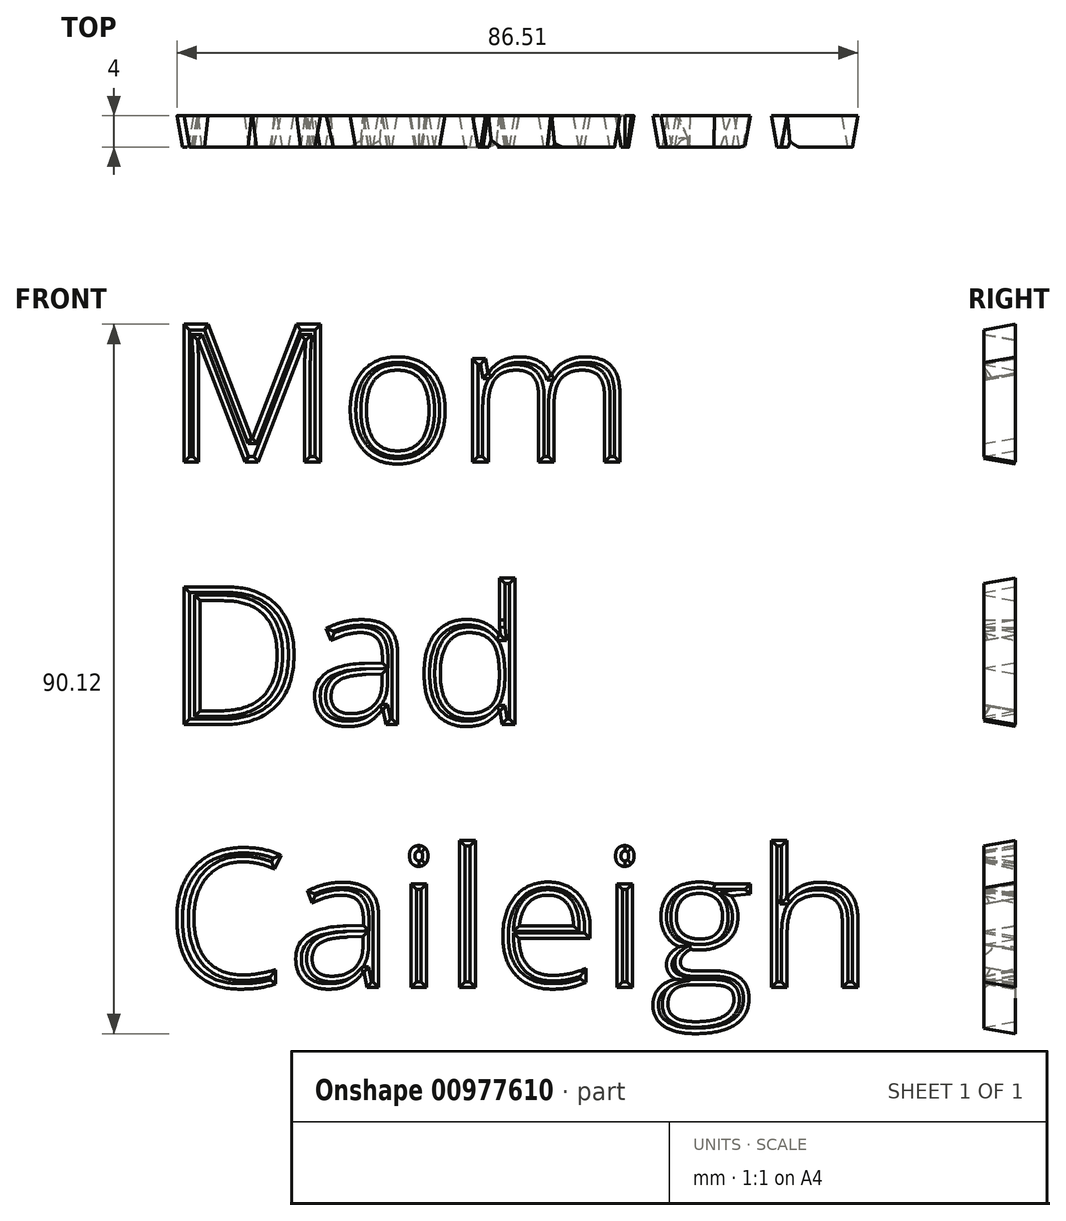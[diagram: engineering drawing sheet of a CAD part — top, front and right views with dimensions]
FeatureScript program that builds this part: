
annotation { "Feature Type Name" : "Feature", "Feature Type Description" : "" }
export const myFeature = defineFeature(function(context is Context, id is Id, definition is map)
    precondition{}
    {
        {
            var Q0;
            Q0=qCreatedBy(makeId("Front.planeOp"),FACE);
            var sketch = newSketch(context, id + "F0", { "sketchPlane" : qUnion([Q0])});
            skText(sketch, "E0", { "text": "Mom\nDad\nCaileigh", "fontName": "OpenSans-Regular.ttf"});
            const initialGuessF0  = {"E0": [-0.05865, 0.03476, 1, 0, 0.01766]};
            skSetInitialGuess(sketch, initialGuessF0);
            skSolve(sketch);
        }
        {
            var Q0;
            Q0 = qSketchRegion(id + "F0", true);
            extrude(context, id + "F1", {"entities" : qUnion([Q0]), "depth" : 4 * mm, "offsetDistance" : 25 * mm, "hasDraft" : true, "draftAngle" : 10 * degree, "draftPullDirection" : true});
        }
    });
